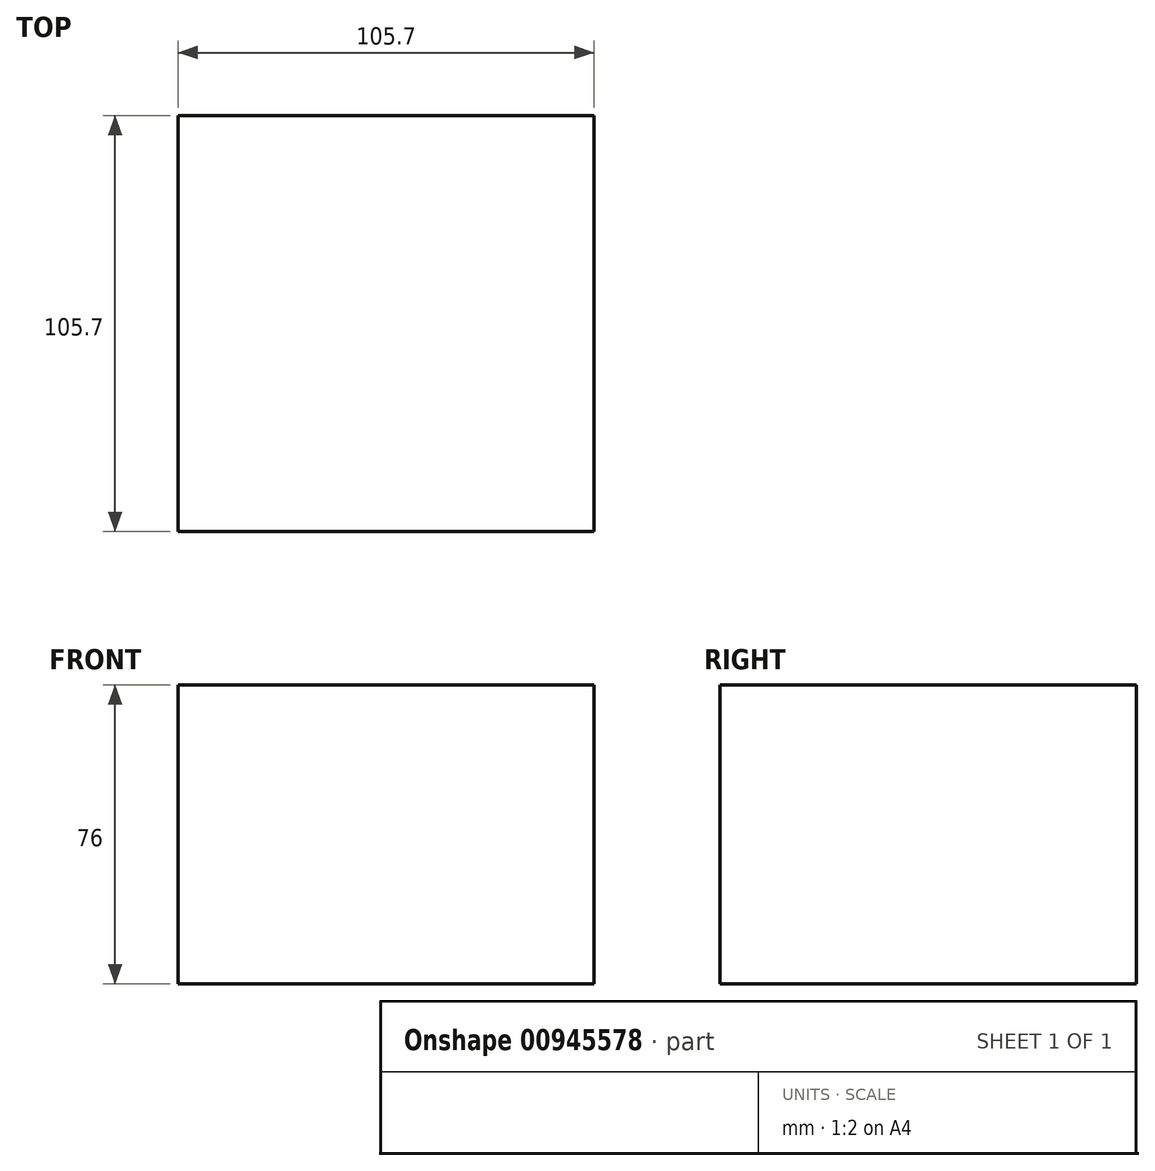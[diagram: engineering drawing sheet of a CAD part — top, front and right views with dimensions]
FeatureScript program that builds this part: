
annotation { "Feature Type Name" : "Feature", "Feature Type Description" : "" }
export const myFeature = defineFeature(function(context is Context, id is Id, definition is map)
    precondition{}
    {
        {
            var Q0;
            Q0=qCreatedBy(makeId("Top.planeOp"),FACE);
            var sketch = newSketch(context, id + "F0", { "sketchPlane" : qUnion([Q0])});
            skLineSegment(sketch, "E0.bottom", {"start": v(-70.2, -52.95) * mm, "end": v(35.5, -52.95) * mm});
            skLineSegment(sketch, "E0.top", {"start": v(-70.2, 52.75) * mm, "end": v(35.5, 52.75) * mm});
            skLineSegment(sketch, "E0.left", {"start": v(-70.2, -52.95) * mm, "end": v(-70.2, 52.75) * mm});
            skLineSegment(sketch, "E0.right", {"start": v(35.5, -52.95) * mm, "end": v(35.5, 52.75) * mm});
            skSolve(sketch);
        }
        {
            var Q0;
            Q0=makeQuery(id+"F0.imprint","IMPRINT",FACE,{"disambiguationData":[TD([[makeQuery(id+"F0.imprint","IMPRINT",EDGE,{"derivedFrom":sQuery(id+"F0.wireOp",EDGE,"E0.bottom")}),1.0]])]});
            extrude(context, id + "F1", {"entities" : qUnion([Q0]), "depth" : 76 * mm, "offsetDistance" : 25 * mm});
        }
    });
